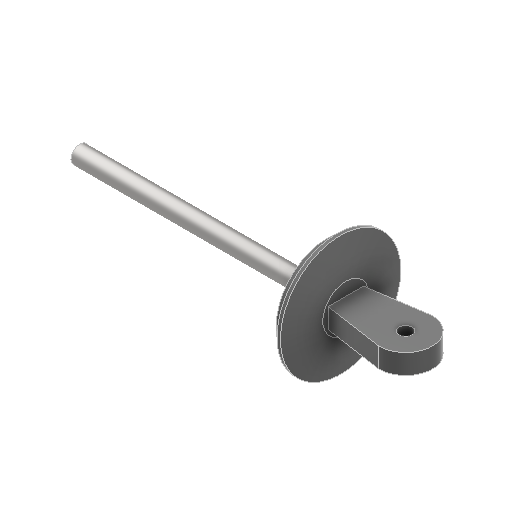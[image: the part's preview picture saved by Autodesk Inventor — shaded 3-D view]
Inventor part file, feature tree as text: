
AUTODESK INVENTOR PART (.ipt)
format: ipt  version: 2025 (Build 290162000, 162)  size: 147,456 bytes
history: native  units: in
note: dims shown in document units (in); Inventor stores cm internally (conversion verified against a paired STEP export)
features: sketch x3, extrude x2, projected_geometry x2, fillet x1, revolve x1
ambient origin geometry x8: Origin, YZ Plane, XZ Plane, XY Plane, X Axis, Y Axis, Z Axis, Center Point
bodies: Solid1 (feature_tree)
feature tree (9):
  extrude  "Extrusion1"  Depth=0.4724in
  extrude  "Extrusion2"  Depth=0.1772in TaperAngle=0.0deg
  fillet  "Fillet1"  Radius=0.1575in
  revolve  "Revolution1"  [1 undecoded]
  sketch  "Sketch1"  dims[d0=0.1181in d1=0.4724in]
  sketch  "Sketch2"  dims[d2=0.1575in d3=0.1772in d4=0.0in d5=0.1575in]
  projected_geometry  "Projected Loop1"
  sketch  "Sketch4"  dims[d6=2.3622in d7=0.0in d8=0.0787in d12=90.0deg d13=0.453in]
  projected_geometry  "Projected Loop3"
note: 1 required parameter value undecoded (feature->parameter linkage not recoverable at this tier; creation-order binding heuristic only, values carry confidence <= 0.55)
